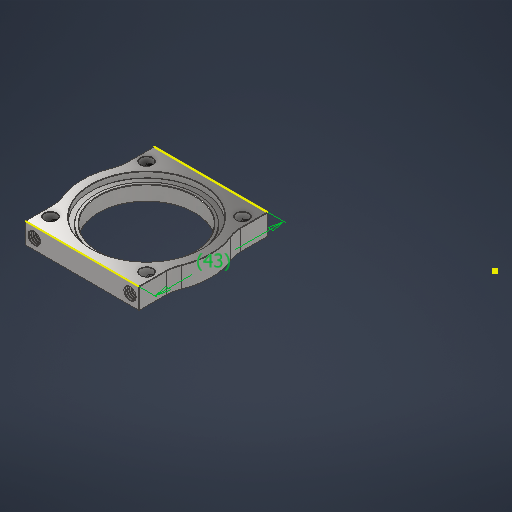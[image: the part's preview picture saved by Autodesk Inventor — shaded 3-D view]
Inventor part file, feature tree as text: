
AUTODESK INVENTOR PART (.ipt)
format: ipt  version: 2025 (Build 290162000, 162)  size: 1,367,040 bytes
history: native  units: in
note: dims shown in document units (in); Inventor stores cm internally (conversion verified against a paired STEP export)
features: sketch x1
ambient origin geometry x8: Origin, YZ Plane, XZ Plane, XY Plane, X Axis, Y Axis, Z Axis, Center Point
bodies: Solid1 (feature_tree), Solid2 (feature_tree)
feature tree (1):
  sketch  "Sketch1"  dims[d1=1.6929in]
